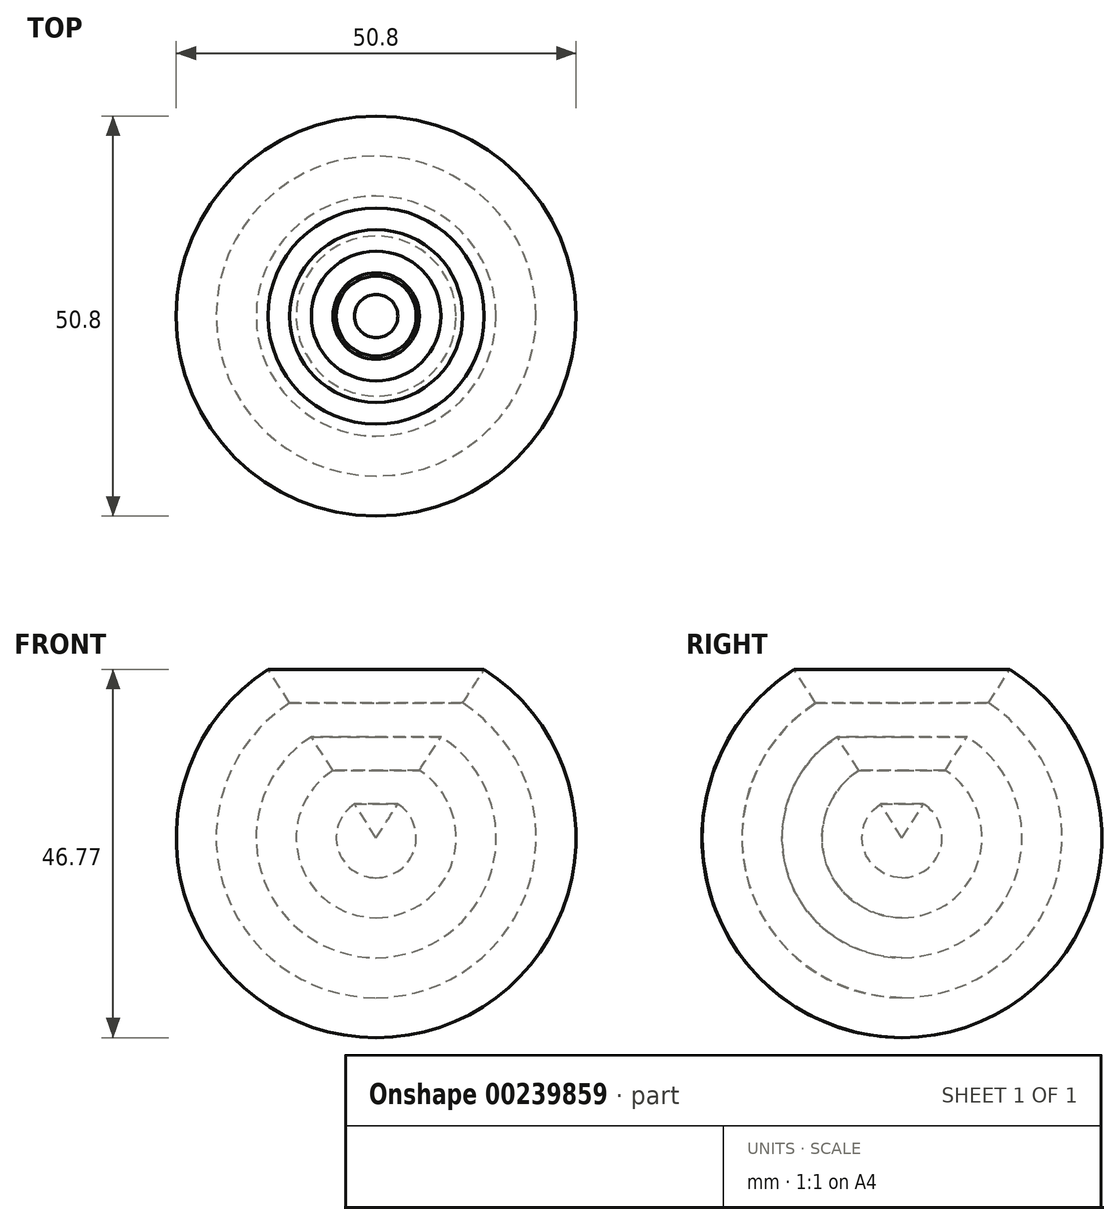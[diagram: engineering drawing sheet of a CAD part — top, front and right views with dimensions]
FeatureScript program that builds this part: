
annotation { "Feature Type Name" : "Feature", "Feature Type Description" : "" }
export const myFeature = defineFeature(function(context is Context, id is Id, definition is map)
    precondition{}
    {
        {
            var Q0;
            Q0=qCreatedBy(makeId("Right.planeOp"),FACE);
            var sketch = newSketch(context, id + "F0", { "sketchPlane" : qUnion([Q0])});
            skCircle(sketch, "E0", {"center": v(0, 0) * mm, "radius": 20.32 * mm});
            skCircle(sketch, "E1", {"center": v(0, 0) * mm, "radius": 25.4 * mm});
            skLineSegment(sketch, "E2", {"start": v(0, 25.4) * mm, "end": v(0, -25.4) * mm});
            skLineSegment(sketch, "E3", {"start": v(-19.9, 30.99) * mm, "end": v(0, 0) * mm});
            skCircle(sketch, "E4", {"center": v(0, 0) * mm, "radius": 15.24 * mm});
            skCircle(sketch, "E5", {"center": v(0, 0) * mm, "radius": 10.16 * mm});
            skCircle(sketch, "E6", {"center": v(0, 0) * mm, "radius": 5.08 * mm});
            skSolve(sketch);
        }
        {
            var Q0;
            {var subQ0=sQuery(id+"F0.wireOp",EDGE,"E3");var subQ1=sQuery(id+"F0.wireOp",EDGE,"E2");var subQ2=makeQuery(id+"F0.imprint","INTERSECT",VERTEX,{"derivedFrom":[subQ1,subQ0]});Q0=makeQuery(id+"F0.imprint","IMPRINT",FACE,{"disambiguationData":[TD([[makeQuery(id+"F0.imprint","IMPRINT",EDGE,{"disambiguationData":[TD([[subQ2,-1.0]])],"derivedFrom":subQ1}),-1.0]])]});}
            var Q1;
            Q1=sQuery(id+"F0.wireOp",EDGE,"E2");
            revolve(context, id + "F1", {"entities" : qUnion([Q0]), "axis" : qUnion([Q1]), "revolveType" : RevolveType.FULL});
        }
        {
            var Q0;
            {var subQ0=sQuery(id+"F0.wireOp",EDGE,"E5");var subQ1=sQuery(id+"F0.wireOp",EDGE,"E2");var subQ2=makeQuery(id+"F0.imprint","INTERSECT",VERTEX,{"disambiguationData":[OD(1.0)],"derivedFrom":[subQ1,subQ0]});Q0=makeQuery(id+"F0.imprint","IMPRINT",FACE,{"disambiguationData":[TD([[makeQuery(id+"F0.imprint","IMPRINT",EDGE,{"disambiguationData":[TD([[subQ2,-1.0]])],"derivedFrom":subQ1}),-1.0]])]});}
            var Q1;
            Q1=sQuery(id+"F0.wireOp",EDGE,"E2");
            revolve(context, id + "F2", {"entities" : qUnion([Q0]), "axis" : qUnion([Q1]), "revolveType" : RevolveType.FULL});
        }
        {
            var Q0;
            {var subQ0=sQuery(id+"F0.wireOp",EDGE,"E3");var subQ1=sQuery(id+"F0.wireOp",EDGE,"E0");var subQ2=makeQuery(id+"F0.imprint","INTERSECT",VERTEX,{"derivedFrom":[subQ1,subQ0]});Q0=makeQuery(id+"F0.imprint","IMPRINT",FACE,{"disambiguationData":[TD([[makeQuery(id+"F0.imprint","IMPRINT",EDGE,{"disambiguationData":[TD([[subQ2,-1.0]])],"derivedFrom":subQ1}),-1.0]])]});}
            var Q1;
            Q1=sQuery(id+"F0.wireOp",EDGE,"E2");
            revolve(context, id + "F3", {"entities" : qUnion([Q0]), "axis" : qUnion([Q1]), "revolveType" : RevolveType.FULL});
        }
    });
